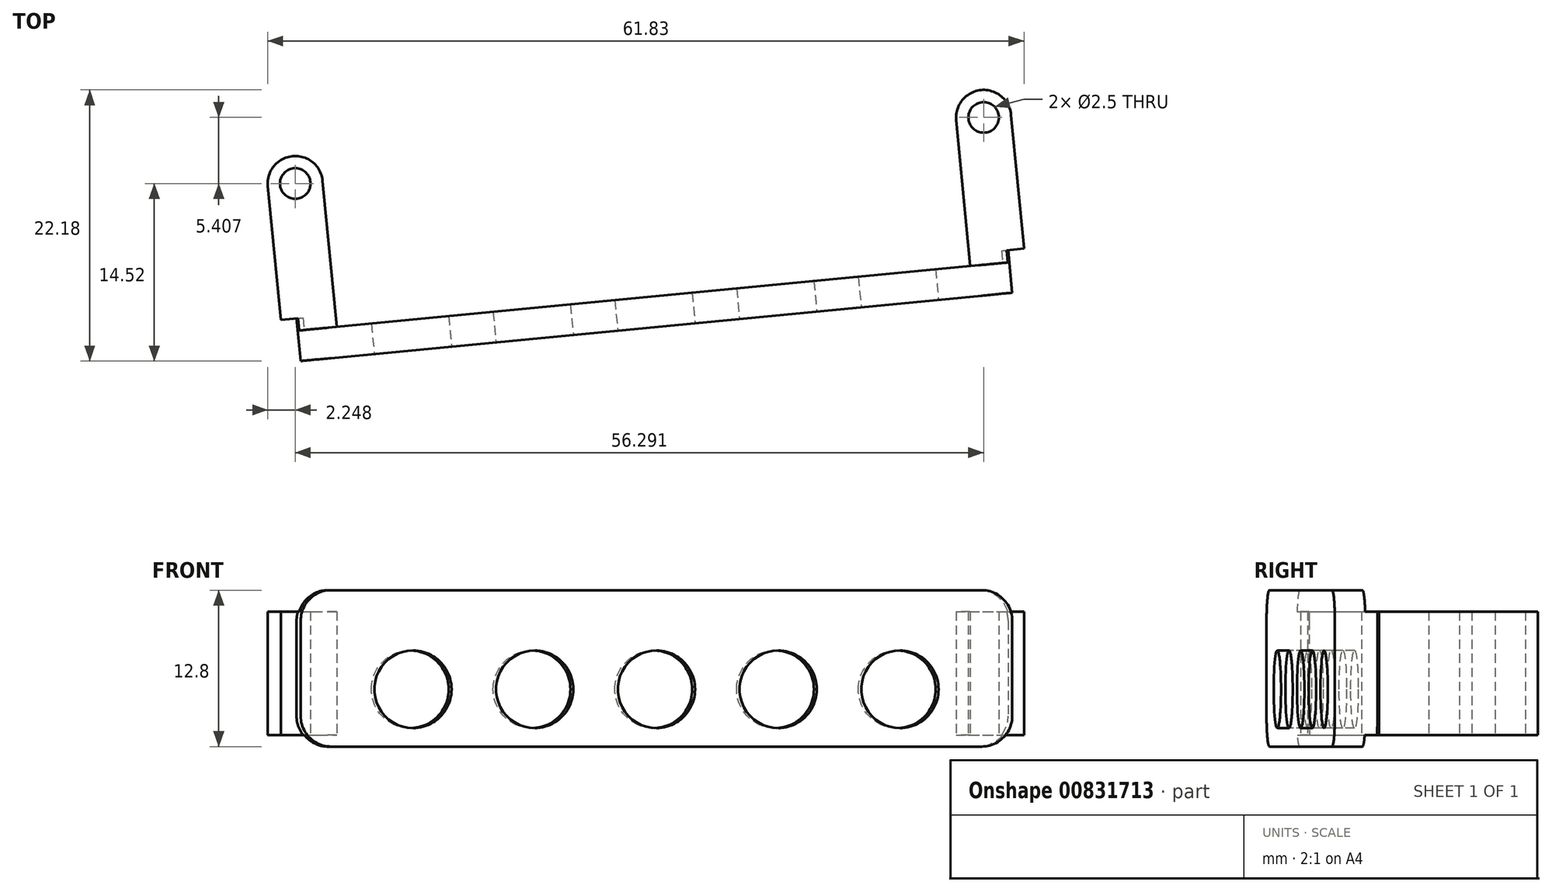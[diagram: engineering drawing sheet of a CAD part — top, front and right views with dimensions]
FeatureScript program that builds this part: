
annotation { "Feature Type Name" : "Feature", "Feature Type Description" : "" }
export const myFeature = defineFeature(function(context is Context, id is Id, definition is map)
    precondition{}
    {
        {
            var Q0;
            Q0=qCreatedBy(makeId("Top.planeOp"),FACE);
            var sketch = newSketch(context, id + "F0", { "sketchPlane" : qUnion([Q0])});
            skLineSegment(sketch, "E0.left", {"start": v(-31.77, 11.51) * mm, "end": v(-30.39, -2.92) * mm});
            skLineSegment(sketch, "E0.right", {"start": v(-27.3, 11.95) * mm, "end": v(-26.14, 0) * mm});
            skLineSegment(sketch, "E1.left", {"start": v(24.52, 16.92) * mm, "end": v(25.67, 4.98) * mm});
            skLineSegment(sketch, "E1.right", {"start": v(29, 17.35) * mm, "end": v(30.39, 2.92) * mm});
            skLineSegment(sketch, "E2", {"start": v(-30.39, -2.92) * mm, "end": v(30.39, 2.92) * mm});
            skLineSegment(sketch, "E3", {"start": v(-26.14, 0) * mm, "end": v(25.67, 4.98) * mm});
            skLineSegment(sketch, "E4", {"start": v(-31.77, 11.51) * mm, "end": v(-27.3, 11.95) * mm, "construction": true});
            skArc(sketch, "E5", {"start": v(-27.3, 11.95) * mm, "mid": v(-29.75, 13.97) * mm, "end": v(-31.77, 11.51) * mm});
            skLineSegment(sketch, "E6", {"start": v(24.52, 16.92) * mm, "end": v(29, 17.35) * mm, "construction": true});
            skArc(sketch, "E7", {"start": v(29, 17.35) * mm, "mid": v(26.54, 19.38) * mm, "end": v(24.52, 16.92) * mm});
            skSolve(sketch);
        }
        {
            var Q0;
            Q0=makeQuery(id+"F0.imprint","IMPRINT",FACE,{"disambiguationData":[TD([[makeQuery(id+"F0.imprint","IMPRINT",EDGE,{"derivedFrom":sQuery(id+"F0.wireOp",EDGE,"E0.left")}),1.0]])]});
            extrude(context, id + "F1", {"entities" : qUnion([Q0]), "depth" : 12.8 * mm, "offsetDistance" : 25.4 * mm});
        }
        {
            var Q0;
            Q0=makeQuery(id+"F1.opExtrude","SWEPT_FACE",FACE,{"disambiguationData":[OSD([sQuery(id+"F0.wireOp",EDGE,"E2")])]});
            var sketch = newSketch(context, id + "F2", { "sketchPlane" : qUnion([Q0])});
            skLineSegment(sketch, "E8.bottom", {"start": v(-26.73, 12.8) * mm, "end": v(26.72, 12.8) * mm});
            skLineSegment(sketch, "E8.top", {"start": v(-26.73, 0) * mm, "end": v(26.72, 0) * mm});
            skLineSegment(sketch, "E8.left", {"start": v(-29.23, 10.3) * mm, "end": v(-29.23, 2.5) * mm});
            skLineSegment(sketch, "E8.right", {"start": v(29.22, 10.3) * mm, "end": v(29.22, 2.5) * mm});
            skArc(sketch, "E9.filletArc", {"start": v(-29.23, 2.5) * mm, "mid": v(-28.5, 0.73) * mm, "end": v(-26.73, 0) * mm});
            skArc(sketch, "E10.filletArc", {"start": v(26.72, 0) * mm, "mid": v(28.5, 0.73) * mm, "end": v(29.22, 2.5) * mm});
            skArc(sketch, "E11.filletArc", {"start": v(29.22, 10.3) * mm, "mid": v(28.5, 12.07) * mm, "end": v(26.72, 12.8) * mm});
            skArc(sketch, "E12.filletArc", {"start": v(-26.73, 12.8) * mm, "mid": v(-28.5, 12.07) * mm, "end": v(-29.23, 10.3) * mm});
            skPoint(sketch, "E13", {"position": v(0, 12.8) * mm});
            skSolve(sketch);
        }
        {
            var Q0;
            {var subQ0=sQuery(id+"F2.wireOp",EDGE,"E12.filletArc");Q0=makeQuery(id+"F2.imprint","IMPRINT",FACE,{"disambiguationData":[TD([[makeQuery(id+"F2.imprint","IMPRINT",EDGE,{"derivedFrom":subQ0}),-1.0]])]});}
            var Q1;
            {var subQ0=sQuery(id+"F2.wireOp",EDGE,"E9.filletArc");Q1=makeQuery(id+"F2.imprint","IMPRINT",FACE,{"disambiguationData":[TD([[makeQuery(id+"F2.imprint","IMPRINT",EDGE,{"derivedFrom":subQ0}),-1.0]])]});}
            var Q2;
            {var subQ0=sQuery(id+"F2.wireOp",EDGE,"E11.filletArc");Q2=makeQuery(id+"F2.imprint","IMPRINT",FACE,{"disambiguationData":[TD([[makeQuery(id+"F2.imprint","IMPRINT",EDGE,{"derivedFrom":subQ0}),-1.0]])]});}
            var Q3;
            {var subQ0=sQuery(id+"F2.wireOp",EDGE,"E10.filletArc");Q3=makeQuery(id+"F2.imprint","IMPRINT",FACE,{"disambiguationData":[TD([[makeQuery(id+"F2.imprint","IMPRINT",EDGE,{"derivedFrom":subQ0}),-1.0]])]});}
            extrude(context, id + "F3", {"entities" : qUnion([Q0, Q1, Q2, Q3]), "operationType" : NewBodyOperationType.REMOVE, "oppositeDirection" : true, "depth" : 3.5 * mm, "offsetDistance" : 25.4 * mm});
        }
        {
            var Q0;
            Q0=makeQuery(id+"F1.opExtrude","SWEPT_FACE",FACE,{"disambiguationData":[OSD([sQuery(id+"F0.wireOp",EDGE,"E1.right")])]});
            var sketch = newSketch(context, id + "F4", { "sketchPlane" : qUnion([Q0])});
            skLineSegment(sketch, "E14.bottom", {"start": v(2.5, 12.8) * mm, "end": v(21.4, 12.8) * mm});
            skLineSegment(sketch, "E14.top", {"start": v(2.5, 11.05) * mm, "end": v(21.4, 11.05) * mm});
            skLineSegment(sketch, "E14.left", {"start": v(2.5, 12.8) * mm, "end": v(2.5, 11.05) * mm});
            skLineSegment(sketch, "E14.right", {"start": v(21.4, 12.8) * mm, "end": v(21.4, 11.05) * mm});
            skLineSegment(sketch, "E15.bottom", {"start": v(2.5, 0) * mm, "end": v(24.78, 0) * mm});
            skLineSegment(sketch, "E15.top", {"start": v(2.5, 0.95) * mm, "end": v(24.78, 0.95) * mm});
            skLineSegment(sketch, "E15.left", {"start": v(2.5, 0) * mm, "end": v(2.5, 0.95) * mm});
            skLineSegment(sketch, "E15.right", {"start": v(24.78, 0) * mm, "end": v(24.78, 0.95) * mm});
            skSolve(sketch);
        }
        {
            var Q0;
            Q0 = qSketchRegion(id + "F4", true);
            extrude(context, id + "F5", {"entities" : qUnion([Q0]), "operationType" : NewBodyOperationType.REMOVE, "endBound" : BoundingType.THROUGH_ALL, "oppositeDirection" : true, "depth" : 25.4 * mm, "offsetDistance" : 25.4 * mm});
        }
        {
            var Q0;
            {var subQ0=sQuery(id+"F0.wireOp",EDGE,"E0.left");Q0=makeQuery(id+"F5.boolean.opBoolean","COPY",FACE,{"disambiguationData":[TD([makeQuery(id+"F1.opExtrude","SWEPT_FACE",FACE,{"disambiguationData":[OSD([subQ0])]})])],"derivedFrom":makeQuery(id+"F5.opExtrude","SWEPT_FACE",FACE,{"disambiguationData":[OSD([sQuery(id+"F4.wireOp",EDGE,"E15.top")])]})});}
            var sketch = newSketch(context, id + "F6", { "sketchPlane" : qUnion([Q0])});
            skPoint(sketch, "E16", {"position": v(26.76, -17.14) * mm});
            skPoint(sketch, "E17", {"position": v(-29.53, -11.73) * mm});
            skSolve(sketch);
        }
        {
            var Q0;
            Q0=sQuery(id+"F6.wireOp",VERTEX,"E16");
            var Q1;
            Q1=sQuery(id+"F6.wireOp",VERTEX,"E17");
            var Q2;
            Q2=makeQuery(id+"F1.opExtrude","SWEPT_BODY",BODY,{"disambiguationData":[OSD([sQuery(id+"F0.wireOp",EDGE,"E0.left"),sQuery(id+"F0.wireOp",EDGE,"E0.right"),sQuery(id+"F0.wireOp",EDGE,"E1.left"),sQuery(id+"F0.wireOp",EDGE,"E1.right"),sQuery(id+"F0.wireOp",EDGE,"E2"),sQuery(id+"F0.wireOp",EDGE,"E3"),sQuery(id+"F0.wireOp",EDGE,"E5"),sQuery(id+"F0.wireOp",EDGE,"E7")])]});
            hole(context, id + "F7", {"style" : HoleStyle.SIMPLE, "endStyle" : HoleEndStyle.THROUGH, "holeDiameter" : 2.5 * mm, "majorDiameter" : 5 * mm, "isTappedThrough" : true, "tappedDepth" : 12.7 * mm, "tapClearance" : 3, "locations" : qUnion([Q0, Q1]), "scope" : qUnion([Q2])});
        }
        {
            var Q0;
            Q0=makeQuery(id+"F1.opExtrude","SWEPT_FACE",FACE,{"disambiguationData":[OSD([sQuery(id+"F0.wireOp",EDGE,"E2")])]});
            var sketch = newSketch(context, id + "F8", { "sketchPlane" : qUnion([Q0])});
            skPoint(sketch, "E18", {"position": v(-20, 4.7) * mm});
            skPoint(sketch, "E19.1.0.0", {"position": v(-10, 4.7) * mm});
            skPoint(sketch, "E19.2.0.0", {"position": v(0, 4.7) * mm});
            skPoint(sketch, "E19.3.0.0", {"position": v(10, 4.7) * mm});
            skPoint(sketch, "E19.4.0.0", {"position": v(20, 4.7) * mm});
            skLineSegment(sketch, "E19.direction1", {"start": v(-20, 4.69) * mm, "end": v(-10, 4.69) * mm, "construction": true});
            skLineSegment(sketch, "E20", {"start": v(-29.22, 4.69) * mm, "end": v(29.22, 4.69) * mm, "construction": true});
            skSolve(sketch);
        }
        {
            var Q0;
            Q0=sQuery(id+"F8.wireOp",VERTEX,"E18");
            var Q1;
            Q1=sQuery(id+"F8.wireOp",VERTEX,"E19.1.0.0");
            var Q2;
            Q2=sQuery(id+"F8.wireOp",VERTEX,"E19.2.0.0");
            var Q3;
            Q3=sQuery(id+"F8.wireOp",VERTEX,"E19.3.0.0");
            var Q4;
            Q4=sQuery(id+"F8.wireOp",VERTEX,"E19.4.0.0");
            var Q5;
            Q5=makeQuery(id+"F1.opExtrude","SWEPT_BODY",BODY,{"disambiguationData":[OSD([sQuery(id+"F0.wireOp",EDGE,"E0.left"),sQuery(id+"F0.wireOp",EDGE,"E0.right"),sQuery(id+"F0.wireOp",EDGE,"E1.left"),sQuery(id+"F0.wireOp",EDGE,"E1.right"),sQuery(id+"F0.wireOp",EDGE,"E2"),sQuery(id+"F0.wireOp",EDGE,"E3"),sQuery(id+"F0.wireOp",EDGE,"E5"),sQuery(id+"F0.wireOp",EDGE,"E7")])]});
            hole(context, id + "F9", {"style" : HoleStyle.SIMPLE, "endStyle" : HoleEndStyle.THROUGH, "holeDiameter" : 6.35 * mm, "majorDiameter" : 5 * mm, "isTappedThrough" : true, "tappedDepth" : 12.7 * mm, "tapClearance" : 3, "locations" : qUnion([Q0, Q1, Q2, Q3, Q4]), "scope" : qUnion([Q5])});
        }
    });
